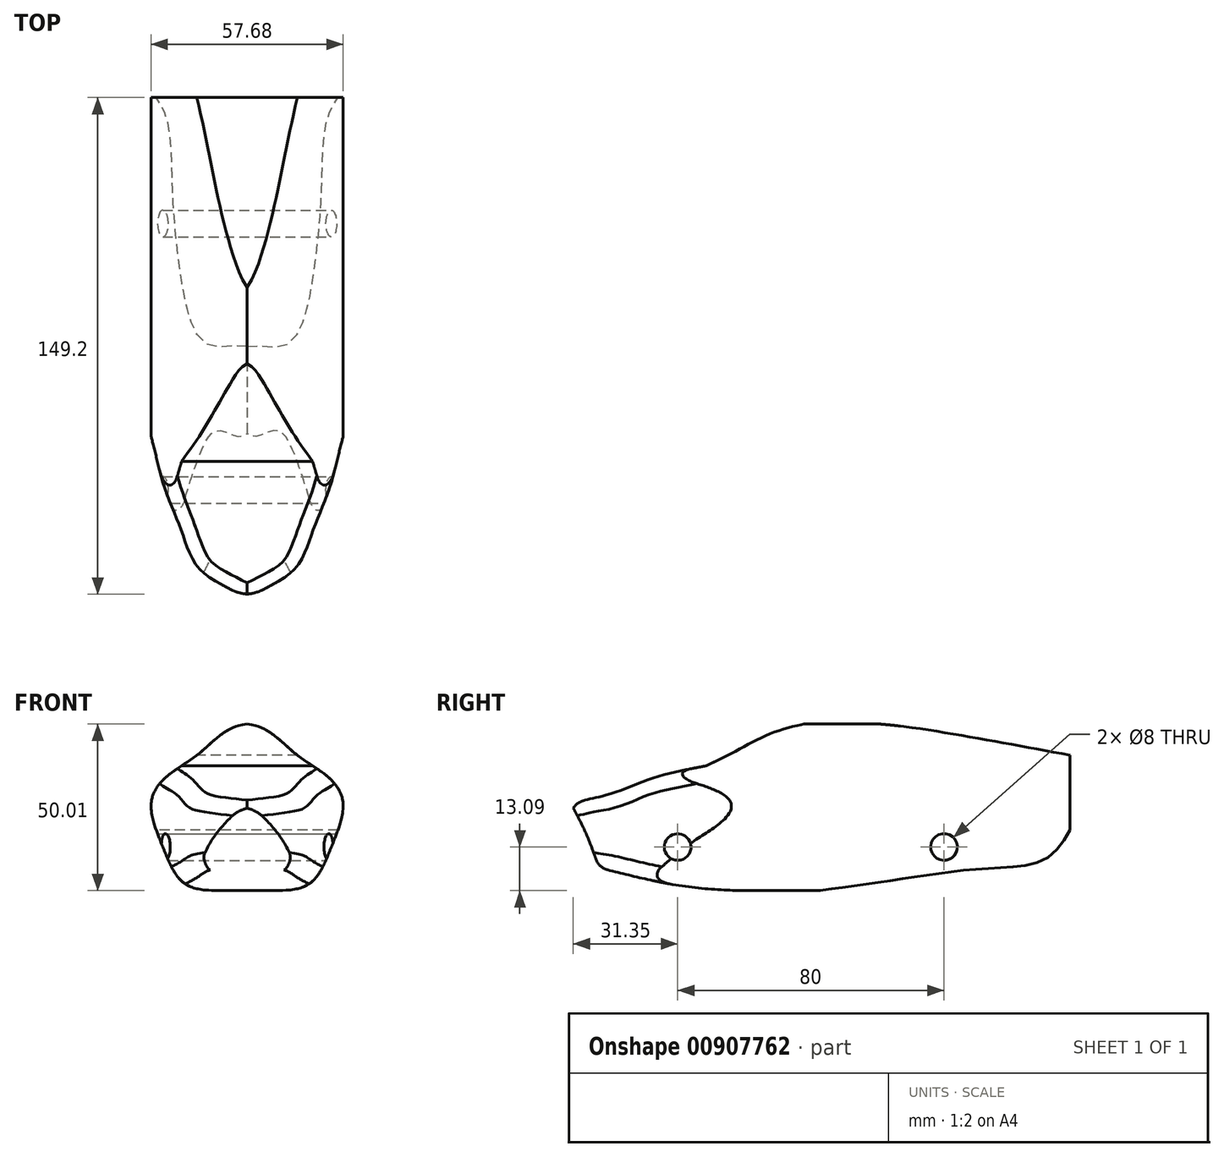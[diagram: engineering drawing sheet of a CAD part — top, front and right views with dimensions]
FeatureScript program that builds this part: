
annotation { "Feature Type Name" : "Feature", "Feature Type Description" : "" }
export const myFeature = defineFeature(function(context is Context, id is Id, definition is map)
    precondition{}
    {
        {
            var Q0;
            Q0=qCreatedBy(makeId("Front.planeOp"),FACE);
            var sketch = newSketch(context, id + "F0", { "sketchPlane" : qUnion([Q0])});
            skFitSpline(sketch, "E0", {"points": [v(0, -26.15) * mm, v(-9.38, -26.18) * mm, v(-18.94, -23.95) * mm, v(-25.3, -13.12) * mm, v(-28.81, 0) * mm, v(-24.35, 7.9) * mm, v(-14.16, 15.22) * mm, v(0, 23.82) * mm], "startDerivative": vector(-73.76, 2.59) * mm, "endDerivative": vector(115.6, 11.3) * mm});
            skFitSpline(sketch, "E1.MirrorCS", {"points": [v(0, -26.15) * mm, v(9.38, -26.18) * mm, v(18.94, -23.95) * mm, v(25.3, -13.12) * mm, v(28.81, 0) * mm, v(24.35, 7.9) * mm, v(14.16, 15.22) * mm, v(0, 23.82) * mm], "startDerivative": vector(73.76, 2.59) * mm, "endDerivative": vector(-115.6, 11.3) * mm});
            skLineSegment(sketch, "E2.bottom", {"start": v(-41.4, 32.03) * mm, "end": v(44.65, 32.03) * mm});
            skLineSegment(sketch, "E2.top", {"start": v(-41.4, -37.09) * mm, "end": v(44.65, -37.09) * mm});
            skLineSegment(sketch, "E2.left", {"start": v(-41.4, 32.03) * mm, "end": v(-41.4, -37.09) * mm});
            skLineSegment(sketch, "E2.right", {"start": v(44.65, 32.03) * mm, "end": v(44.65, -37.09) * mm});
            skSolve(sketch);
        }
        {
            var Q0;
            Q0=qCreatedBy(makeId("Right.planeOp"),FACE);
            var sketch = newSketch(context, id + "F1", { "sketchPlane" : qUnion([Q0])});
            skFitSpline(sketch, "E3", {"points": [v(0, 24.25) * mm, v(19.43, 23.93) * mm, v(45.01, 20.46) * mm, v(77.85, 14.46) * mm], "startDerivative": vector(65.5, 0.9) * mm, "endDerivative": vector(88.87, -16.68) * mm});
            skFitSpline(sketch, "E4", {"points": [v(0, -26.6) * mm, v(28.59, -22.49) * mm, v(51.33, -19.65) * mm, v(70.27, -16.8) * mm, v(77.85, -7.96) * mm], "startDerivative": vector(98.63, 13.88) * mm, "endDerivative": vector(31.25, 54.63) * mm});
            skLineSegment(sketch, "E5", {"start": v(77.85, 14.46) * mm, "end": v(77.85, -7.96) * mm});
            skFitSpline(sketch, "E6", {"points": [v(0, 24.25) * mm, v(-11.83, 21.1) * mm, v(-22.57, 15.72) * mm, v(-31.41, 11.3) * mm], "startDerivative": vector(-34.74, -7.26) * mm, "endDerivative": vector(-27.87, -13.43) * mm});
            skFitSpline(sketch, "E7", {"points": [v(-31.41, 11.3) * mm, v(-47.83, 7.51) * mm, v(-57.62, 3.72) * mm, v(-72.15, 0) * mm], "startDerivative": vector(-48.65, -9.38) * mm, "endDerivative": vector(-45.12, -9.94) * mm});
            skFitSpline(sketch, "E8", {"points": [v(-72.15, 0) * mm, v(-67.73, -8.6) * mm, v(-63.62, -19.33) * mm], "startDerivative": vector(9.57, -17.34) * mm, "endDerivative": vector(7.51, -21.26) * mm});
            skFitSpline(sketch, "E9", {"points": [v(-63.62, -19.33) * mm, v(-47.83, -23.12) * mm, v(-31.41, -25.65) * mm, v(0, -26.6) * mm], "startDerivative": vector(54.52, -13.7) * mm, "endDerivative": vector(83.31, -0.77) * mm});
            skSolve(sketch);
        }
        {
            var Q0;
            Q0=makeQuery(id+"F1.imprint","IMPRINT",FACE,{"disambiguationData":[TD([[makeQuery(id+"F1.imprint","IMPRINT",EDGE,{"derivedFrom":sQuery(id+"F1.wireOp",EDGE,"E3")}),-1.0]])]});
            extrude(context, id + "F2", {"entities" : qUnion([Q0]), "endBound" : BoundingType.SYMMETRIC, "depth" : 60 * mm, "offsetDistance" : 25 * mm});
        }
        {
            var Q0;
            Q0=makeQuery(id+"F0.imprint","IMPRINT",FACE,{"disambiguationData":[TD([[makeQuery(id+"F0.imprint","IMPRINT",EDGE,{"derivedFrom":sQuery(id+"F0.wireOp",EDGE,"E0")}),1.0]])]});
            extrude(context, id + "F3", {"entities" : qUnion([Q0]), "operationType" : NewBodyOperationType.REMOVE, "endBound" : BoundingType.SYMMETRIC, "oppositeDirection" : true, "depth" : 160 * mm, "offsetDistance" : 25 * mm});
        }
        {
            var Q0;
            Q0=qCreatedBy(makeId("Top.planeOp"),FACE);
            var sketch = newSketch(context, id + "F4", { "sketchPlane" : qUnion([Q0])});
            skFitSpline(sketch, "E10", {"points": [v(0, -72.15) * mm, v(-7.99, -68.22) * mm, v(-15.16, -62.71) * mm, v(-19.95, -51.7) * mm, v(-24.73, -39.5) * mm, v(-28.81, -23.96) * mm], "startDerivative": vector(-46.64, 17.8) * mm, "endDerivative": vector(-18.08, 68.47) * mm});
            skLineSegment(sketch, "E11", {"start": v(-28.81, -23.96) * mm, "end": v(-57.76, -23.96) * mm});
            skLineSegment(sketch, "E12", {"start": v(-57.76, -23.96) * mm, "end": v(-57.76, -90.47) * mm});
            skLineSegment(sketch, "E13", {"start": v(-57.76, -90.47) * mm, "end": v(0, -90.47) * mm});
            skLineSegment(sketch, "E14", {"start": v(0, -90.47) * mm, "end": v(0, -72.15) * mm});
            skLineSegment(sketch, "E15.MirrorCS", {"start": v(28.81, -23.96) * mm, "end": v(57.76, -23.96) * mm});
            skFitSpline(sketch, "E16.MirrorCS", {"points": [v(0, -72.15) * mm, v(7.99, -68.22) * mm, v(15.16, -62.71) * mm, v(19.95, -51.7) * mm, v(24.73, -39.5) * mm, v(28.81, -23.96) * mm], "startDerivative": vector(46.64, 17.8) * mm, "endDerivative": vector(18.08, 68.47) * mm});
            skLineSegment(sketch, "E17.MirrorCS", {"start": v(57.76, -23.96) * mm, "end": v(57.76, -90.47) * mm});
            skLineSegment(sketch, "E18.MirrorCS", {"start": v(57.76, -90.47) * mm, "end": v(0, -90.47) * mm});
            skSolve(sketch);
        }
        {
            var Q0;
            Q0=makeQuery(id+"F4.imprint","IMPRINT",FACE,{"disambiguationData":[TD([[makeQuery(id+"F4.imprint","IMPRINT",EDGE,{"derivedFrom":sQuery(id+"F4.wireOp",EDGE,"E10")}),1.0]])]});
            var Q1;
            Q1=makeQuery(id+"F4.imprint","IMPRINT",FACE,{"disambiguationData":[TD([[makeQuery(id+"F4.imprint","IMPRINT",EDGE,{"derivedFrom":sQuery(id+"F4.wireOp",EDGE,"E14")}),-1.0]])]});
            extrude(context, id + "F5", {"entities" : qUnion([Q0, Q1]), "operationType" : NewBodyOperationType.REMOVE, "endBound" : BoundingType.SYMMETRIC, "oppositeDirection" : true, "depth" : 50 * mm, "offsetDistance" : 25 * mm});
        }
        {
            var Q0;
            Q0=makeQuery(id+"F5.boolean.opBoolean","INTERSECT",EDGE,{"derivedFrom":[makeQuery(id+"F2.opExtrude","SWEPT_FACE",FACE,{"disambiguationData":[OSD([sQuery(id+"F1.wireOp",EDGE,"E7")])]}),makeQuery(id+"F5.opExtrude","SWEPT_FACE",FACE,{"disambiguationData":[OSD([sQuery(id+"F4.wireOp",EDGE,"E16.MirrorCS")])]})]});
            var Q1;
            Q1=makeQuery(id+"F5.boolean.opBoolean","INTERSECT",EDGE,{"derivedFrom":[makeQuery(id+"F2.opExtrude","SWEPT_FACE",FACE,{"disambiguationData":[OSD([sQuery(id+"F1.wireOp",EDGE,"E7")])]}),makeQuery(id+"F5.opExtrude","SWEPT_FACE",FACE,{"disambiguationData":[OSD([sQuery(id+"F4.wireOp",EDGE,"E10")])]})]});
            var Q2;
            Q2=makeQuery(id+"F2.opExtrude","SWEPT_EDGE",EDGE,{"disambiguationData":[OSD([sQuery(id+"F1.wireOp",EDGE,"E8"),sQuery(id+"F1.wireOp",EDGE,"E9")])]});
            var Q3;
            Q3=makeQuery(id+"F5.boolean.opBoolean","INTERSECT",EDGE,{"derivedFrom":[makeQuery(id+"F2.opExtrude","SWEPT_FACE",FACE,{"disambiguationData":[OSD([sQuery(id+"F1.wireOp",EDGE,"E9")])]}),makeQuery(id+"F5.opExtrude","SWEPT_FACE",FACE,{"disambiguationData":[OSD([sQuery(id+"F4.wireOp",EDGE,"E16.MirrorCS")])]})]});
            var Q4;
            Q4=makeQuery(id+"F5.boolean.opBoolean","INTERSECT",EDGE,{"derivedFrom":[makeQuery(id+"F2.opExtrude","SWEPT_FACE",FACE,{"disambiguationData":[OSD([sQuery(id+"F1.wireOp",EDGE,"E9")])]}),makeQuery(id+"F5.opExtrude","SWEPT_FACE",FACE,{"disambiguationData":[OSD([sQuery(id+"F4.wireOp",EDGE,"E10")])]})]});
            fillet(context, id + "F6", {"entities" : qUnion([Q0, Q1, Q2, Q3, Q4]), "radius" : 5 * mm, "tangentPropagation" : true, "allowEdgeOverflow" : false});
        }
        {
            var Q0;
            Q0=qCreatedBy(makeId("Right.planeOp"),FACE);
            var sketch = newSketch(context, id + "F7", { "sketchPlane" : qUnion([Q0])});
            skCircle(sketch, "E19", {"center": v(-40, -13.1) * mm, "radius": 4 * mm});
            skCircle(sketch, "E20.MirrorC", {"center": v(40, -13.1) * mm, "radius": 4 * mm});
            skSolve(sketch);
        }
        {
            var Q0;
            Q0 = qSketchRegion(id + "F7", true);
            extrude(context, id + "F8", {"entities" : qUnion([Q0]), "operationType" : NewBodyOperationType.REMOVE, "endBound" : BoundingType.SYMMETRIC, "oppositeDirection" : true, "depth" : 70 * mm, "offsetDistance" : 25 * mm});
        }
    });
